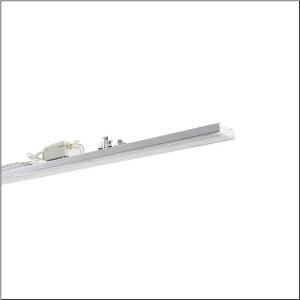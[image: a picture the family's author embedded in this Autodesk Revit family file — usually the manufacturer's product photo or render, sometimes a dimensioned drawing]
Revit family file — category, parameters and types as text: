
# Revit family: licross_r__11_recessed_mo_51te10dn495g_4ea1
name_source: partatom
category: Lighting Fixtures
units: mm (PartAtom-declared; Revit-internal decimal feet)

## family parameters
Cut with Voids When Loaded = No
Host = Face
Light Source = No
Part Type = Normal
Room Calculation Point = No
Round Connector Dimension = Use Diameter
Shared = No

## types (1)
- --- (1 x LED, 9960 lm, 56.7 W, 4000K)
    Apparent Load = 57 VA
    CIE Flux Codes = 50 81 96 100 100
    Color Rendering = 80
    Color Temperature = 4000K
    Default Elevation = 1800 mm
    Description = Licross® 11 Recessed MO, luminaire insert, of sheet steel, galvanised, coil coated, white, length: 1.500mm, width: 66mm, height: 67mm, LED rated luminous flux: 9.960lm, light colour: 840, SDCM (Standard Deviation of Colour Matching)MacAdam ≤ 2 SDCM (initial), control gear: DALI 2, with plug, 5-pole, with phase selection, mains connection: 220..240V, AC, 50/60Hz, rated input power: 57W, internal wiring halogen-free, primary optical cover: cover, of PMMA, light emission: direct distribution, primary light characteristic: symmetric, protection rating (complete): IP54, insulation class (complete): insulation class I (protective earthing), certification: CE, ENEC, VDE, UKCA, protection symbol: D if used in an environment with non-conductive dust loads with corresponding accessories, impact resistance: IK06, permissible ambient temperature for indoor applications: -25..+35°C, corresponds to IFS (International Featured Standards) requirements for safety and quality in the food industry, reducing of maximum allowable ambient temperature of 5°C with ceiling mounting, LABS conformity tested according to VDMA 24364:2018-05, packaging unit: 1 piece
    Height = 58 mm
    Lamp = 1 x LED
    Lamp Light Flux = 9960 lm
    Lamp Power = 56.7 W
    Lamp count = 1
    Length = 1500 mm
    Luminous efficacy = 176 lm/W
    Manufacturer = Siteco
    ModVariant = No
    Model = 51TE10DN495G
    Mounting Place = Ceiling
    Mounting Type = Pendant
    Number of Poles = 1
    OnlyDefault = Yes
    Power Factor = 1
    Product Name = Licross® 11 Recessed MO
    Product group = luminaire insert | ceiling pendant
    ProductGroupID = 901
    Protection Class = Protection class I
    Protection Degree = IP 54
    RLX_Detail_Level = 1
    RLX_Emergency_Light_Flux = 0 lm
    RLX_Emergency_Type = 0
    RLX_Emergency_Type_DB = No
    RlxData = <blob elided: 24445 chars, md5=0c5e8476>
    Socket = socket
    Standby Power = 0 W
    System Light Flux = 9960 lm
    System Power = 57 W
    Type Comments = factory setting: luminous flux: 100 % | dim-lin: 254 | 378 mA
    Type Image = l_1296930.jpg
    URL = http://relux.com
    VarID = @adj_105355
    Voltage = 0 V
    Weight = 0.00 kg
    Width = 66 mm

## geometry (parser evidence)
native form markers: Blend x4, Sweep x11
no freeform markers — native parametric forms only
